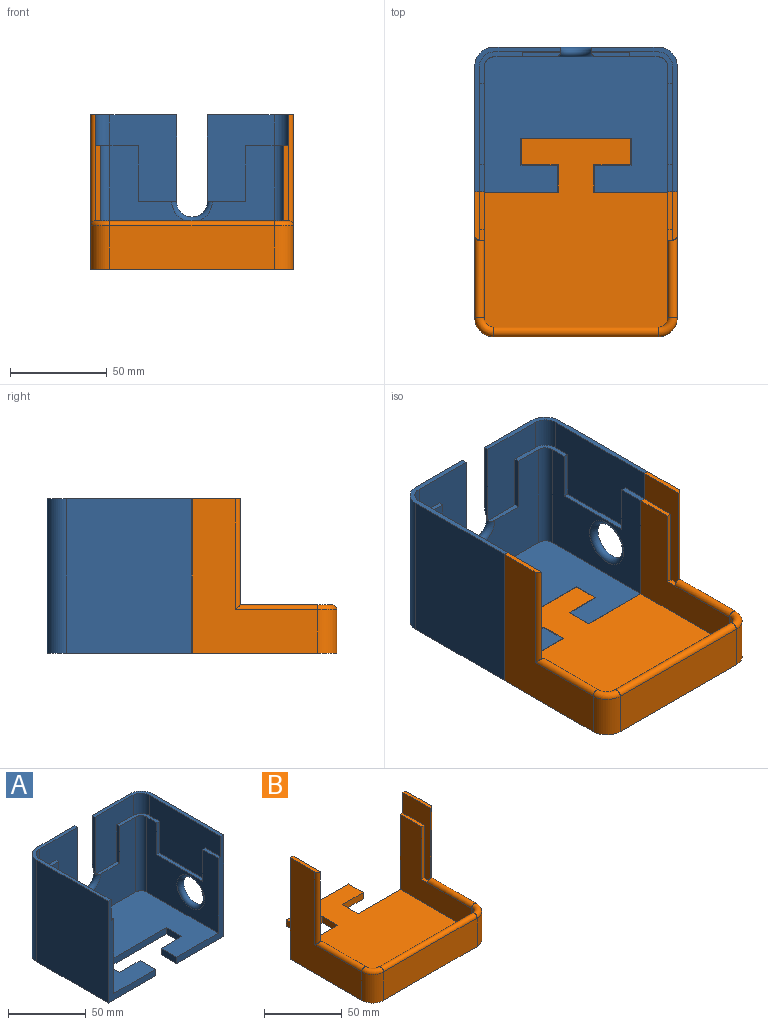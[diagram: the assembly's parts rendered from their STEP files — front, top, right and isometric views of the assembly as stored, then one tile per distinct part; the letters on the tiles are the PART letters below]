
ASSEMBLY  parts=2 mates=1
PART A: 47 faces, bbox 105x75x80 mm
  f0: plane 22.25x16.5mm, normal (0,0,1), area 83.9mm2, adj f1,f4,f9,f26,f32,f38,f42,f44
  f1: plane 85x59mm, normal (0,-1,0), area 3232.3mm2, adj f0,f2,f6,f23,f37,f38,f39,f40
  f2: torus R=10.5mm, axis (0,1,0), area 248.4mm2, adj f1,f21,f34,f35,f37,f39
  f3: plane 75x44.5mm, normal (0,0,1), area 283.1mm2, adj f4,f18,f19,f21,f26,f34,f44,f46
  f4: plane 45x34.5mm, normal (0,-1,0), area 1124.8mm2, adj f0,f3,f34,f37,f38,f44
  f5: plane 14x2.5mm, normal (0,0,1), area 35mm2, adj f9,f18,f26,f31
  f6: plane 22.25x16.5mm, normal (0,0,1), area 83.9mm2, adj f1,f7,f24,f25,f29,f40,f41,f43
  f7: plane 65x59mm, normal (-1,0,0), area 2294.1mm2, adj f6,f8,f23,f27,f28,f29,f30,f36
  f8: plane 80x43mm, normal (0,-1,0), area 550mm2, adj f7,f10,f11,f20,f22,f23,f24,f27
  f9: plane 65x59mm, normal (1,0,0), area 2785mm2, adj f0,f5,f18,f23,f31,f32,f33,f42
  f10: plane 75x44.5mm, normal (0,0,1), area 283.1mm2, adj f8,f20,f21,f24,f25,f35,f43,f45
  f11: plane 14x5mm, normal (-1,0,0), area 70mm2, adj f8,f12,f22,f23
  f12: plane 19x5mm, normal (0,1,0), area 95mm2, adj f11,f13,f22,f23
  f13: plane 14x5mm, normal (-1,0,0), area 70mm2, adj f12,f14,f22,f23
  f14: plane 57x5mm, normal (0,-1,0), area 285mm2, adj f13,f15,f22,f23
  f15: plane 14x5mm, normal (1,0,0), area 70mm2, adj f14,f16,f22,f23
  f16: plane 19x5mm, normal (0,1,0), area 95mm2, adj f15,f17,f22,f23
  f17: plane 14x5mm, normal (1,0,0), area 70mm2, adj f16,f18,f22,f23
  f18: plane 80x43mm, normal (0,-1,0), area 550mm2, adj f3,f5,f9,f17,f19,f22,f23,f26
  f19: plane 80x65mm, normal (-1,0,0), area 5200mm2, adj f3,f18,f22,f46
  f20: plane 80x65mm, normal (1,0,0), area 4709.1mm2, adj f8,f10,f22,f36,f45
  f21: plane 85x80mm, normal (0,1,0), area 5883.5mm2, adj f2,f3,f10,f22,f34,f35,f45,f46
  f22: plane 105x75mm, normal (0,0,-1), area 6768.1mm2, adj f8,f11,f12,f13,f14,f15,f16,f17
  f23: plane 95x70mm, normal (0,0,1), area 5575.3mm2, adj f1,f7,f8,f9,f11,f12,f13,f14
  f24: plane 65x41mm, normal (-1,0,0), area 2090mm2, adj f6,f8,f10,f27,f28,f29,f30,f43
  f25: plane 45x34.5mm, normal (0,-1,0), area 1124.8mm2, adj f6,f10,f35,f39,f40,f43
  f26: plane 65x41mm, normal (1,0,0), area 2090mm2, adj f0,f3,f5,f18,f31,f32,f33,f44
  f27: plane 14x2.5mm, normal (0,0,1), area 35mm2, adj f7,f8,f24,f28
  f28: plane 25x2.5mm, normal (0,1,0), area 62.5mm2, adj f7,f24,f27,f30
  f29: plane 25x2.5mm, normal (0,-1,0), area 62.5mm2, adj f6,f7,f24,f30
  f30: plane 42x2.5mm, normal (0,0,1), area 105mm2, adj f7,f24,f28,f29
  f31: plane 25x2.5mm, normal (0,1,0), area 62.5mm2, adj f5,f9,f26,f33
  f32: plane 25x2.5mm, normal (0,-1,0), area 62.5mm2, adj f0,f9,f26,f33
  f33: plane 42x2.5mm, normal (0,0,1), area 105mm2, adj f9,f26,f31,f32
  f34: plane 45x2.5mm, normal (1,0,0), area 106.2mm2, adj f2,f3,f4,f21
  f35: plane 45x2.5mm, normal (-1,0,0), area 106.2mm2, adj f2,f10,f21,f25
  f36: torus R=12.5mm, axis (-1,0,0), area 538.3mm2, adj f7,f20
  f37: plane 19.75x2.5mm, normal (0,0,1), area 48mm2, adj f1,f2,f4,f38
  f38: plane 29x2.5mm, normal (1,0,0), area 72.5mm2, adj f0,f1,f4,f37
  f39: plane 19.75x2.5mm, normal (0,0,1), area 48mm2, adj f1,f2,f25,f40
  f40: plane 29x2.5mm, normal (-1,0,0), area 72.5mm2, adj f1,f6,f25,f39
  f41: cylinder r=5mm len=59mm, axis (0,0,-1), area 463.4mm2, adj f1,f6,f7,f23
  f42: cylinder r=5mm len=59mm, axis (0,0,1), area 463.4mm2, adj f0,f1,f9,f23
  f43: cylinder r=7.5mm len=16mm, axis (0,0,-1), area 188.5mm2, adj f6,f10,f24,f25
  f44: cylinder r=7.5mm len=16mm, axis (0,0,-1), area 188.5mm2, adj f0,f3,f4,f26
  f45: cylinder r=10mm len=80mm, axis (0,0,1), area 1256.6mm2, adj f10,f20,f21,f22
  f46: cylinder r=10mm len=80mm, axis (0,0,-1), area 1256.6mm2, adj f3,f19,f21,f22
PART B: 40 faces, bbox 106.6x103.6x80 mm
  f0: cylinder r=2.5mm len=42.5mm, axis (0,1,0), area 317.7mm2, adj f10,f14,f34,f35,f36
  f1: plane 80x43.25mm, normal (0,1,0), area 551.3mm2, adj f2,f10,f13,f14,f17,f20,f21,f25
  f2: plane 14.25x5mm, normal (-1,0,0), area 71.3mm2, adj f1,f3,f13,f17
  f3: plane 19x5mm, normal (0,-1,0), area 95mm2, adj f2,f4,f13,f17
  f4: plane 13.5x5mm, normal (-1,0,0), area 67.5mm2, adj f3,f5,f13,f17
  f5: plane 56.5x5mm, normal (0,1,0), area 282.5mm2, adj f4,f6,f13,f17
  f6: plane 13.5x5mm, normal (1,0,0), area 67.5mm2, adj f5,f7,f13,f17
  f7: plane 19x5mm, normal (0,-1,0), area 95mm2, adj f6,f8,f13,f17
  f8: plane 14.25x5mm, normal (1,0,0), area 71.3mm2, adj f7,f9,f13,f17
  f9: plane 80x43.25mm, normal (0,1,0), area 551.2mm2, adj f8,f12,f13,f16,f17,f18,f19,f23
  f10: plane 80x65mm, normal (-1,0,0), area 2756.2mm2, adj f0,f1,f13,f21,f26,f35
  f11: plane 85x22.5mm, normal (0,-1,0), area 1912.5mm2, adj f13,f26,f27,f33
  f12: plane 80x65mm, normal (1,0,0), area 2756.2mm2, adj f9,f13,f19,f27,f30,f31
  f13: plane 105x102.75mm, normal (0,0,-1), area 8858.5mm2, adj f1,f2,f3,f4,f5,f6,f7,f8
  f14: plane 65x59mm, normal (1,0,0), area 1946.7mm2, adj f0,f1,f17,f24,f25,f29,f37
  f15: plane 85x17.5mm, normal (0,1,0), area 1487.5mm2, adj f17,f28,f29,f33
  f16: plane 65x59mm, normal (-1,0,0), area 1946.7mm2, adj f9,f17,f22,f23,f28,f31,f39
  f17: plane 97.75x95mm, normal (0,0,1), area 7665.6mm2, adj f1,f2,f3,f4,f5,f6,f7,f8
  f18: plane 57.5x25mm, normal (-1,0,0), area 628.2mm2, adj f9,f19,f22,f23,f30,f38,f39
  f19: plane 25x2.5mm, normal (0,0,1), area 61.2mm2, adj f9,f12,f18,f30
  f20: plane 57.5x25mm, normal (1,0,0), area 628.2mm2, adj f1,f21,f24,f25,f35,f36,f37
  f21: plane 25x2.5mm, normal (0,0,1), area 61.2mm2, adj f1,f10,f20,f35
  f22: plane 41.5x2.5mm, normal (0,-1,0), area 103.7mm2, adj f16,f18,f23,f39
  f23: plane 19.5x2.5mm, normal (0,0,1), area 48.7mm2, adj f9,f16,f18,f22
  f24: plane 41.5x2.5mm, normal (0,-1,0), area 103.8mm2, adj f14,f20,f25,f37
  f25: plane 19.5x2.5mm, normal (0,0,1), area 48.7mm2, adj f1,f14,f20,f24
  f26: cylinder r=10mm len=22.5mm, axis (0,0,1), area 353.4mm2, adj f10,f11,f13,f34
  f27: cylinder r=10mm len=22.5mm, axis (0,0,-1), area 353.4mm2, adj f11,f12,f13,f32
  f28: cylinder r=5mm len=17.5mm, axis (0,0,1), area 137.4mm2, adj f15,f16,f17,f32
  f29: cylinder r=5mm len=17.5mm, axis (0,0,-1), area 137.4mm2, adj f14,f15,f17,f34
  f30: cylinder r=2.5mm len=57.5mm, axis (0,0,1), area 219.6mm2, adj f12,f18,f19,f31
  f31: cylinder r=2.5mm len=42.5mm, axis (0,-1,0), area 317.7mm2, adj f12,f16,f30,f32,f38
  f32: torus R=7.5mm, axis (0,0,1), area 92.5mm2, adj f27,f28,f31,f33
  f33: cylinder r=2.5mm len=85mm, axis (-1,0,0), area 667.6mm2, adj f11,f15,f32,f34
  f34: torus R=7.5mm, axis (0,0,1), area 92.5mm2, adj f0,f26,f29,f33
  f35: cylinder r=2.5mm len=57.5mm, axis (0,0,1), area 219.6mm2, adj f0,f10,f20,f21
  f36: plane 2.5x2.5mm, normal (0,1,0), area 4.9mm2, adj f0,f20,f37
  f37: plane 5.5x2.5mm, normal (0,0,1), area 13.7mm2, adj f14,f20,f24,f36
  f38: plane 2.5x2.5mm, normal (0,1,0), area 4.9mm2, adj f18,f31,f39
  f39: plane 5.5x2.5mm, normal (0,0,1), area 13.7mm2, adj f16,f18,f22,f38
PLACE A t=(-12.62,-4.2,33.72)mm
PLACE B t=(-12.62,-79.2,33.72)mm
MATE parallel B.f9 <-> A.f8  axis (0,1,0) through (92.38,-4.2,33.72)mm
